# Revit family: Kältefestpunkt
name_source: partatom
category: HLS-Bauteile
revit_build: Autodesk Revit 2017 (Build: 20190507_1515(x64)
units: mm (PartAtom-declared; Revit-internal decimal feet)

## family parameters
Arbeitsebenenbasiert = Nein
Beim Laden mit Abzugskörper schneiden = Nein
Bemaßung runder Anschluss = Durchmesser verwenden
Gemeinsam genutzt = Ja
Immer vertikal = Nein
Raumberechnungspunkt = Nein
Teiletyp = Normal

## types (10) — shared parameters
Dichte = 200 kg/m³
Dämmstärke = 40 mm  [stored 0.131234 ft]
Fabrikat = MEFA
Firma = MEFA Befestigungs- und Montagesysteme GmbH
Mengeneinheit = St
Wärmeleitfähigkeit = 0.037 W/mK
max. Temperaturbeständigkeit = 105 °C
vpe = 1 St

## per-type parameters (varying)
| type | Artikelnummer | Breite Außenhalbringe | D0 | EAN | Gewicht | Gewicht pro Bauteil | Kurztext1 | Kurztext2 | L1 | L2 | Lochabstand | Länge Schale | Rohraußendurchmesser | Rohrschelle | d1 | empf. Unterbau | max. zul. Last axial | max. zul. Last radial |
| Kältefestpunkt Ø 76.1 | 698400076 | 235 mm | 157 mm  [stored 0.515092 ft] | 4250928441133 | 3.75 kg | 3.75 kg | Kältefestpunkt HV 1 | 76.1 mm Iso 40 mm Länge Schale 148 mm | 148 mm | 8 mm  [stored 0.0262467 ft] | 206 mm | 148 mm | 76 mm | MEFA KS ohne Dämmung : MEFA Titan KS Ø157 mm, o.D. | 77 mm | HV1 | 2.70 kN | 5.40 kN |
| Kältefestpunkt Ø 88.9 | 698400089 | 246 mm | 168 mm  [stored 0.551181 ft] | 4250928441140 | 4.02 kg | 4.02 kg | Kältefestpunkt HV 1 | 88.9 mm Iso 40 mm Länge Schale 148 mm | 148 mm | 8 mm  [stored 0.0262467 ft] | 217 mm | 148 mm | 89 mm  [stored 0.291995 ft] | MEFA KS ohne Dämmung : MEFA Titan KS Ø168 mm, o.D. | 90 mm | HV1 | 2.80 kN | 6.30 kN |
| Kältefestpunkt Ø114.3 | 698400114 | 272 mm | 194 mm  [stored 0.636483 ft] | 4250928441157 | 4.66 kg | 4.66 kg | Kältefestpunkt HV 1 | 114.3 mm Iso 40 mm Länge Schale 148 mm | 148 mm | 8 mm  [stored 0.0262467 ft] | 243 mm | 148 mm | 114 mm | MEFA KS ohne Dämmung : MEFA Titan KS Ø194 mm, o.D. | 115 mm  [stored 0.377297 ft] | HV1 | 3.30 kN | 8.00 kN |
| Kältefestpunkt Ø139.7 | 698400140 | 300 mm | 222 mm | 4250928441164 | 5.58 kg | 5.58 kg | Kältefestpunkt HV 1 | 139.7 mm Iso 40 mm Länge Schale 148 mm | 148 mm | 8 mm  [stored 0.0262467 ft] | 271 mm | 148 mm | 140 mm | MEFA KS ohne Dämmung : MEFA Titan KS Ø222 mm, o.D. | 141 mm | HV1 | 4.50 kN | 9.20 kN |
| Kältefestpunkt Ø168.3 | 698400168 | 328 mm | 250 mm  [stored 0.82021 ft] | 4250928441171 | 6.30 kg | 6.30 kg | Kältefestpunkt HV 1 | 168.3 mm Iso 40 mm Länge Schale 148 mm | 148 mm | 8 mm  [stored 0.0262467 ft] | 299 mm | 148 mm | 168 mm  [stored 0.551181 ft] | MEFA KS ohne Dämmung : MEFA Titan KS Ø250 mm, o.D. | 170 mm  [stored 0.557743 ft] | HV1 | 5.60 kN | 10.40 kN |
| Kältefestpunkt Ø219.1 | 698400219 | 378 mm | 300 mm | 4250928441188 | 8.27 kg | 8.27 kg | Kältefestpunkt HV 3 | 219.1 mm Iso 40 mm Länge Schale 204 mm | 204 mm  [stored 0.669291 ft] | 66 mm  [stored 0.216535 ft] | 349 mm | 204 mm | 219 mm  [stored 0.718504 ft] | MEFA KS ohne Dämmung : MEFA Titan KS Ø300 mm, o.D. | 222 mm | HV3 | 8.00 kN | 12.40 kN |
| Kältefestpunkt Ø273 | 698400273 | 433 mm | 355 mm | 4250928441195 | 9.85 kg | 9.85 kg | Kältefestpunkt HV 3 | 273 mm Iso 40 mm Länge Schale 204 mm | 204 mm  [stored 0.669291 ft] | 66 mm  [stored 0.216535 ft] | 404 mm | 204 mm | 273 mm  [stored 0.895669 ft] | MEFA KS ohne Dämmung : MEFA Titan KS Ø355 mm, o.D. | 275 mm | HV3 | 8.90 kN | 13.60 kN |
| Kältefestpunkt Ø323.9 | 698400324 | 484 mm | 406 mm  [stored 1.33202 ft] | 4250928441201 | 11.30 kg | 11.30 kg | Kältefestpunkt HV 4 | 323.9 mm Iso 40 mm Länge Schale 204 mm | 204 mm  [stored 0.669291 ft] | 66 mm  [stored 0.216535 ft] | 455 mm | 204 mm | 324 mm  [stored 1.06299 ft] | MEFA KS ohne Dämmung : MEFA Titan KS Ø406 mm, o.D. | 326 mm | HV4 | 11.10 kN | 16.80 kN |
| Kältefestpunkt Ø355.6 | 698400356 | 516 mm | 438 mm  [stored 1.43701 ft] | 4250928441218 | 12.22 kg | 12.22 kg | Kältefestpunkt HV 4 | 355.6 mm Iso 40 mm Länge Schale 204 mm | 204 mm  [stored 0.669291 ft] | 66 mm  [stored 0.216535 ft] | 487 mm | 204 mm | 356 mm | MEFA KS ohne Dämmung : MEFA Titan KS Ø438 mm, o.D. | 358 mm | HV4 | 12.10 kN | 18.20 kN |
| Kältefestpunkt Ø406.4 | 698400406 | 567 mm | 489 mm  [stored 1.60433 ft] | 4250928441225 | 13.67 kg | 13.67 kg | Kältefestpunkt HV 4 | 406.4 mm Iso 40 mm Länge Schale 204 mm | 204 mm  [stored 0.669291 ft] | 66 mm  [stored 0.216535 ft] | 538 mm | 204 mm | 406 mm  [stored 1.33202 ft] | MEFA KS ohne Dämmung : MEFA Titan KS Ø489 mm, o.D. | 409 mm | HV4 | 13.60 kN | 20.30 kN |

note: [stored X ft] marks values corroborated as IEEE doubles in the binary element streams (Revit-internal decimal feet)
